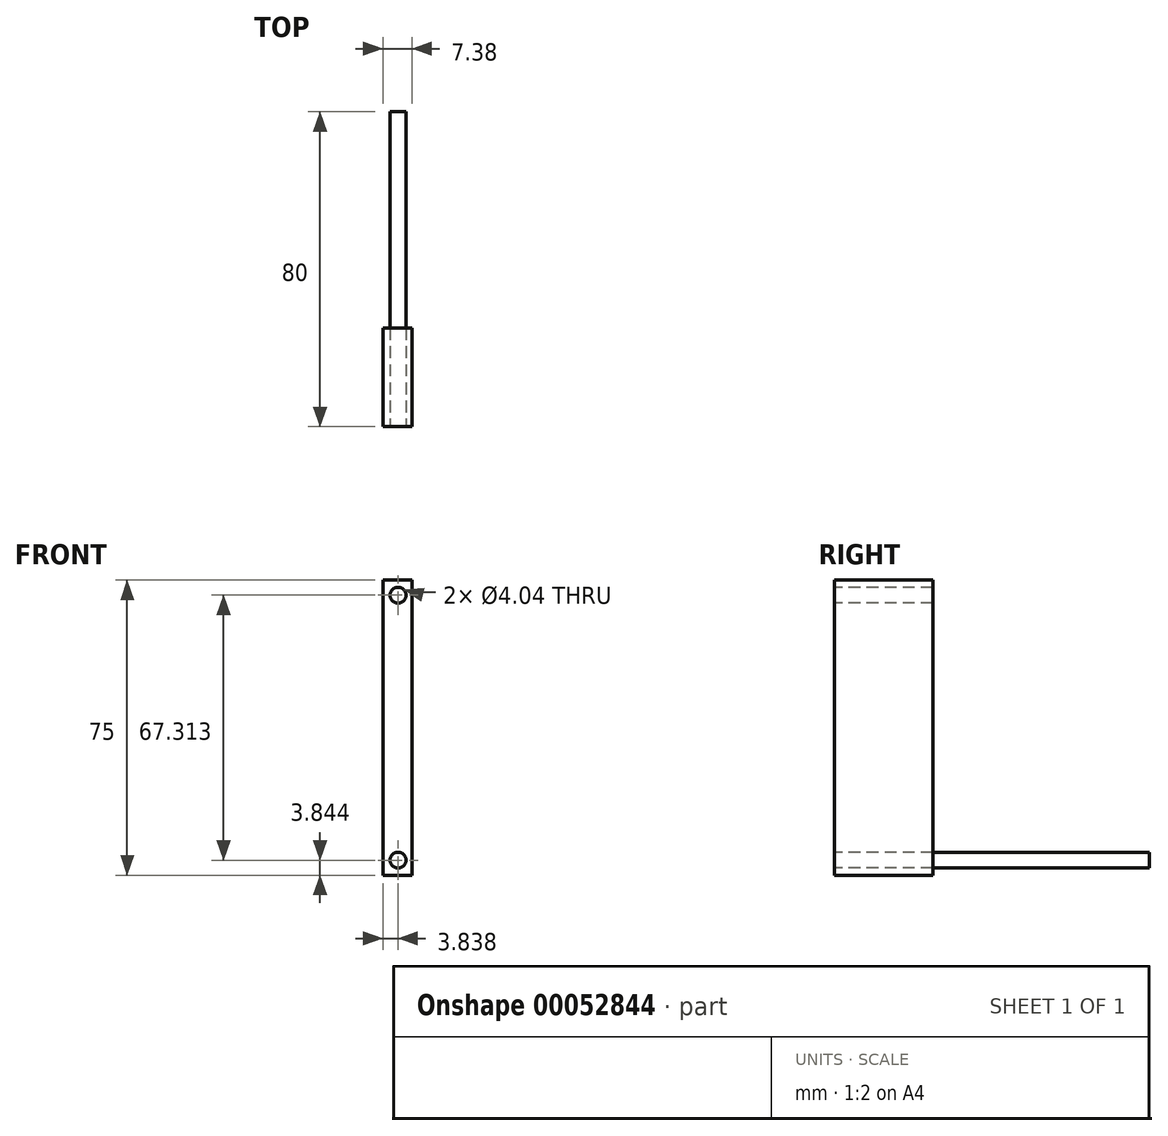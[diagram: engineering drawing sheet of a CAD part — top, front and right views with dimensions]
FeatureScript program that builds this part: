
annotation { "Feature Type Name" : "Feature", "Feature Type Description" : "" }
export const myFeature = defineFeature(function(context is Context, id is Id, definition is map)
    precondition{}
    {
        {
            var Q0;
            Q0=qCreatedBy(makeId("Front.planeOp"),FACE);
            var sketch = newSketch(context, id + "F0", { "sketchPlane" : qUnion([Q0])});
            skLineSegment(sketch, "E0.bottom", {"start": v(3.58, 62.5) * mm, "end": v(-3.8, 62.5) * mm});
            skLineSegment(sketch, "E0.top", {"start": v(3.58, -12.5) * mm, "end": v(-3.8, -12.5) * mm});
            skLineSegment(sketch, "E0.left", {"start": v(3.58, 62.5) * mm, "end": v(3.58, -12.5) * mm});
            skLineSegment(sketch, "E0.right", {"start": v(-3.8, 62.5) * mm, "end": v(-3.8, -12.5) * mm});
            skLineSegment(sketch, "E1.bottom", {"start": v(3.58, 25) * mm, "end": v(-3.8, 25) * mm, "construction": true});
            skLineSegment(sketch, "E1.top", {"start": v(3.58, 25) * mm, "end": v(-3.8, 25) * mm, "construction": true});
            skLineSegment(sketch, "E1.left", {"start": v(3.58, 25) * mm, "end": v(3.58, 25) * mm});
            skLineSegment(sketch, "E1.right", {"start": v(-3.8, 25) * mm, "end": v(-3.8, 25) * mm});
            skCircle(sketch, "E2.0", {"center": v(0.04, 58.66) * mm, "radius": 2.02 * mm});
            skCircle(sketch, "E3.0", {"center": v(0.04, -8.66) * mm, "radius": 2.02 * mm});
            skSolve(sketch);
        }
        {
            var Q0;
            Q0=makeQuery(id+"F0.imprint","IMPRINT",FACE,{"disambiguationData":[TD([[makeQuery(id+"F0.imprint","IMPRINT",EDGE,{"derivedFrom":sQuery(id+"F0.wireOp",EDGE,"E0.bottom")}),1.0]])]});
            extrude(context, id + "F1", {"entities" : qUnion([Q0]), "oppositeDirection" : true, "depth" : 25 * mm});
        }
        {
            var Q0;
            Q0=makeQuery(id+"F0.imprint","IMPRINT",FACE,{"disambiguationData":[TD([[makeQuery(id+"F0.imprint","IMPRINT",EDGE,{"derivedFrom":sQuery(id+"F0.wireOp",EDGE,"E3.0")}),1.0]])]});
            extrude(context, id + "F2", {"entities" : qUnion([Q0]), "oppositeDirection" : true, "depth" : 80 * mm});
        }
    });
